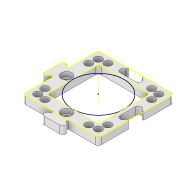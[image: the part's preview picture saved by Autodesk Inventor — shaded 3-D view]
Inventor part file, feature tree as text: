
AUTODESK INVENTOR PART (.ipt)
format: ipt  version: 2022 (Build 260153000, 153)  size: 431,104 bytes
history: native  units: mm
features: sketch x6, projected_geometry x5, extrude x4, mirror x2, pattern_circular x2, other x1, hole x1
ambient origin geometry x8: Origin, YZ Plane, XZ Plane, XY Plane, X Axis, Y Axis, Z Axis, Center Point
bodies: Volumenkörper1 (feature_tree)
feature tree (21):
  extrude  "Extrusion1"  TaperAngle=0.0deg  [1 undecoded]
  mirror  "Mirror6"
  mirror  "Mirror7"
  extrude  "Extrusion13"  TaperAngle=0.0deg  [1 undecoded]
  sketch  "Sketch27"  dims[d9=0.0mm d13=0.0mm]
  extrude  "Extrusion14"  TaperAngle=0.0deg  [1 undecoded]
  other  "Work Axis4"
  pattern_circular  "Circular Pattern6"  [2 undecoded]
  hole  "Hole7"  [1 undecoded]
  extrude  "Extrusion15"  TaperAngle=0.0deg  [1 undecoded]
  pattern_circular  "Circular Pattern7"  [2 undecoded]
  sketch  "Skizze1"  dims[d5=0.0mm d6=0.0mm]
  sketch  "Sketch26"  dims[d7=0.0mm d8=0.0mm]
  projected_geometry  "Projected Loop21"
  projected_geometry  "Projected Loop22"
  sketch  "Sketch28"  dims[d14=0.0mm]
  projected_geometry  "Projected Loop23"
  sketch  "Sketch29"  dims[d20=0.0mm]
  projected_geometry  "Projected Loop24"
  sketch  "Sketch30"  dims[d21=0.0mm d22=0.0mm d23=0.0mm d24=0.0mm d25=3.0mm d26=0.0mm d27=0.0mm d28=0.0mm d29=0.0mm d30=0.0mm d31=0.0mm d32=0.0mm d33=0.0mm d34=0.0mm d46=0.0mm d47=0.0mm d48=0.0mm d49=-10.0mm d50=0.0mm d51=0.0mm d52=0.0mm d53=0.0mm d54=0.0mm d55=0.0mm d56=0.0mm d57=0.0mm d58=0.0mm d59=0.0mm d77=2.65mm d82=2.65mm d222=0.5mm d236=5.3mm d278=25.0mm d279=25.0mm d2=8.0mm d281=8.0mm d282=2.0mm d283=4.9mm d284=20.0mm d4=20.0mm d286=4.9mm d290=20.8mm d292=2.0mm d293=5.5mm d294=14.0mm d295=18.0mm d296=10.0mm d297=1.5mm d298=10.0mm d299=0.0mm d300=2.0mm d301=0.5mm d302=10.0mm d303=0.0mm d308=20.0mm d309=90.0deg d313=6.3mm d314=6.3mm d319=7.78mm d320=4.0mm d322=4.0mm d323=3.2mm d324=6.0mm d325=7.0mm d326=3.0mm d327=90.0deg d328=8.0mm d329=20.594885mm d330=0.0mm d331=0.0mm d332=0.0mm d334=14.0mm d336=10.0mm d337=1.5mm d338=2.0mm d339=0.5mm d340=0.075mm d341=0.075mm d342=0.075mm d343=0.075mm d344=10.0mm d345=0.0mm d346=0.075mm d347=0.0mm d348=20.0mm d349=90.0deg d354=0.075mm d355=3.5mm d356=10.15mm]
  projected_geometry  "Projected Loop25"
note: 9 required parameter values undecoded (feature->parameter linkage not recoverable at this tier; creation-order binding heuristic only, values carry confidence <= 0.55)
